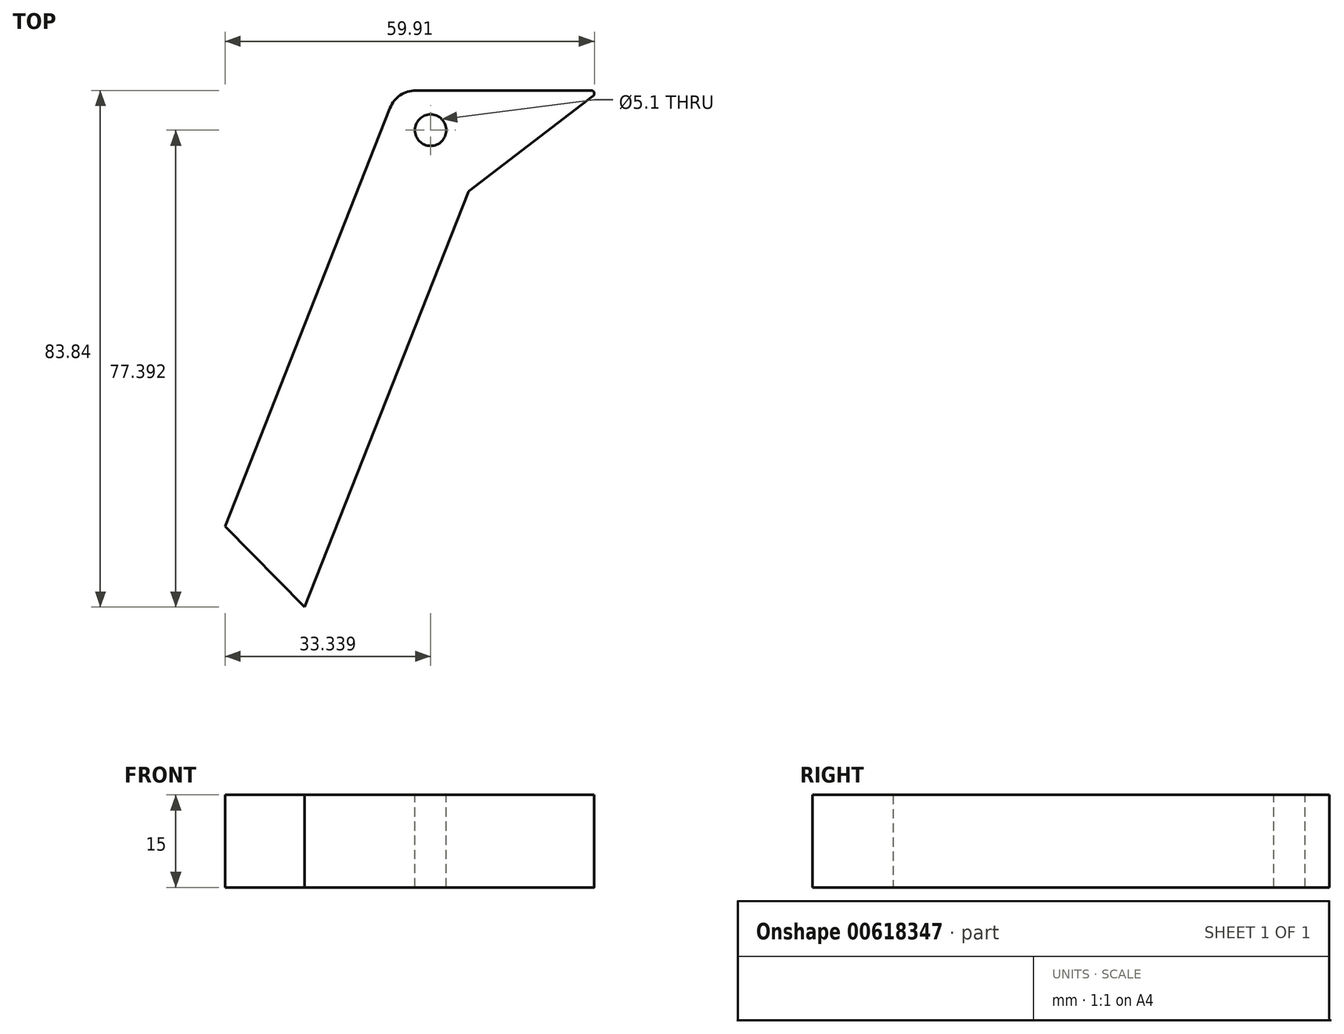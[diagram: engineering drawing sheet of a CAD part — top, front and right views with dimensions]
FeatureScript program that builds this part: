
annotation { "Feature Type Name" : "Feature", "Feature Type Description" : "" }
export const myFeature = defineFeature(function(context is Context, id is Id, definition is map)
    precondition{}
    {
        {
            var Q0;
            Q0=qCreatedBy(makeId("Top.planeOp"),FACE);
            var sketch = newSketch(context, id + "F0", { "sketchPlane" : qUnion([Q0])});
            skLineSegment(sketch, "E0", {"start": v(-12.12, 27.44) * mm, "end": v(16.35, 27.44) * mm});
            skLineSegment(sketch, "E1", {"start": v(16.65, 26.54) * mm, "end": v(-3.5, 11.08) * mm});
            skLineSegment(sketch, "E2", {"start": v(-16.3, 24.59) * mm, "end": v(-43.06, -43.34) * mm});
            skLineSegment(sketch, "E3", {"start": v(-3.65, 10.87) * mm, "end": v(-30.15, -56.4) * mm});
            skLineSegment(sketch, "E4", {"start": v(-43.06, -43.34) * mm, "end": v(-30.15, -56.4) * mm});
            skPoint(sketch, "E5.visualSharp", {"position": v(-15.18, 27.44) * mm});
            skArc(sketch, "E5.filletArc", {"start": v(-12.12, 27.44) * mm, "mid": v(-14.65, 26.66) * mm, "end": v(-16.3, 24.59) * mm});
            skPoint(sketch, "E6.visualSharp", {"position": v(17.82, 27.44) * mm});
            skArc(sketch, "E6.filletArc", {"start": v(16.65, 26.54) * mm, "mid": v(16.82, 27.1) * mm, "end": v(16.35, 27.44) * mm});
            skPoint(sketch, "E7.visualSharp", {"position": v(-3.6, 11) * mm});
            skArc(sketch, "E7.filletArc", {"start": v(-3.5, 11.08) * mm, "mid": v(-3.59, 10.99) * mm, "end": v(-3.65, 10.87) * mm});
            skSolve(sketch);
        }
        {
            var Q0;
            Q0=makeQuery(id+"F0.imprint","IMPRINT",FACE,{"disambiguationData":[TD([[makeQuery(id+"F0.imprint","IMPRINT",EDGE,{"derivedFrom":sQuery(id+"F0.wireOp",EDGE,"E0")}),-1.0]])]});
            extrude(context, id + "F1", {"entities" : qUnion([Q0]), "depth" : 15 * mm, "offsetDistance" : 25 * mm});
        }
        {
            var Q0;
            Q0=makeQuery(id+"F1.opExtrude","CAP_FACE",FACE,{"disambiguationData":[OSD([sQuery(id+"F0.wireOp",EDGE,"E0"),sQuery(id+"F0.wireOp",EDGE,"E1"),sQuery(id+"F0.wireOp",EDGE,"E2"),sQuery(id+"F0.wireOp",EDGE,"E3"),sQuery(id+"F0.wireOp",EDGE,"E4"),sQuery(id+"F0.wireOp",EDGE,"E5.filletArc"),sQuery(id+"F0.wireOp",EDGE,"E6.filletArc"),sQuery(id+"F0.wireOp",EDGE,"E7.filletArc")])],"isStart":false});
            var sketch = newSketch(context, id + "F2", { "sketchPlane" : qUnion([Q0])});
            skCircle(sketch, "E8", {"center": v(-9.72, 21) * mm, "radius": 2.55 * mm});
            skSolve(sketch);
        }
        {
            var Q0;
            Q0=sQuery(id+"F2.wireOp",VERTEX,"E8.center");
            var Q1;
            Q1=makeQuery(id+"F1.opExtrude","SWEPT_BODY",BODY,{"disambiguationData":[OSD([sQuery(id+"F0.wireOp",EDGE,"E0"),sQuery(id+"F0.wireOp",EDGE,"E1"),sQuery(id+"F0.wireOp",EDGE,"E2"),sQuery(id+"F0.wireOp",EDGE,"E3"),sQuery(id+"F0.wireOp",EDGE,"E4"),sQuery(id+"F0.wireOp",EDGE,"E5.filletArc"),sQuery(id+"F0.wireOp",EDGE,"E6.filletArc"),sQuery(id+"F0.wireOp",EDGE,"E7.filletArc")])]});
            hole(context, id + "F3", {"style" : HoleStyle.SIMPLE, "endStyle" : HoleEndStyle.THROUGH, "holeDiameter" : 5.1 * mm, "majorDiameter" : 5 * mm, "isTappedThrough" : true, "tappedDepth" : 12 * mm, "tapClearance" : 3, "locations" : qUnion([Q0]), "scope" : qUnion([Q1])});
        }
    });
